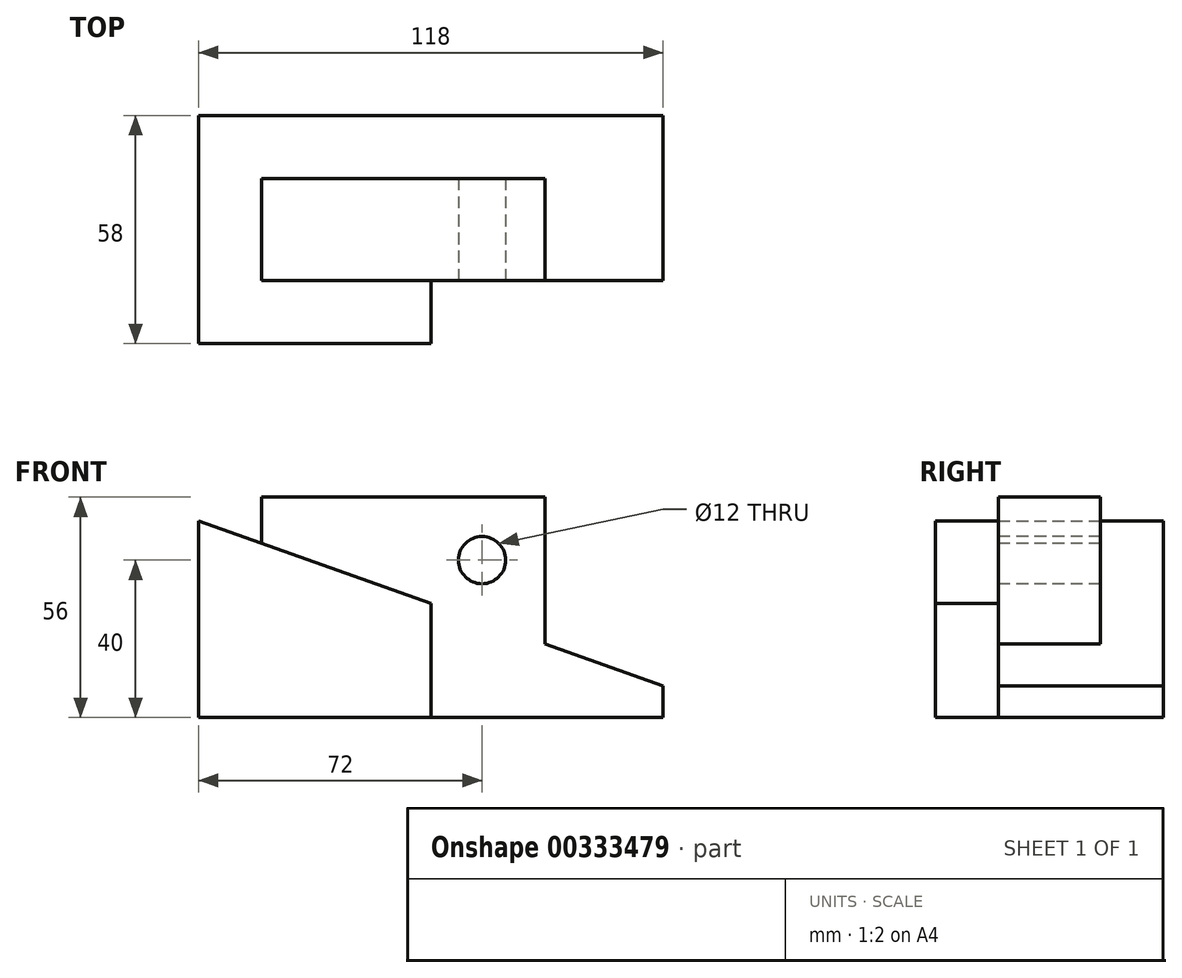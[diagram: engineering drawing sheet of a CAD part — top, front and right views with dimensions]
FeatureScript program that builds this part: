
annotation { "Feature Type Name" : "Feature", "Feature Type Description" : "" }
export const myFeature = defineFeature(function(context is Context, id is Id, definition is map)
    precondition{}
    {
        {
            var Q0;
            Q0=qCreatedBy(makeId("Front.planeOp"),FACE);
            var sketch = newSketch(context, id + "F0", { "sketchPlane" : qUnion([Q0])});
            skLineSegment(sketch, "E0", {"start": v(0, 0) * mm, "end": v(0, 50) * mm});
            skLineSegment(sketch, "E1", {"start": v(0, 50) * mm, "end": v(118, 8) * mm});
            skLineSegment(sketch, "E2", {"start": v(118, 8) * mm, "end": v(118, 0) * mm});
            skLineSegment(sketch, "E3", {"start": v(0, 0) * mm, "end": v(118, 0) * mm});
            skSolve(sketch);
        }
        {
            var Q0;
            Q0=makeQuery(id+"F0.imprint","IMPRINT",FACE,{"disambiguationData":[TD([[makeQuery(id+"F0.imprint","IMPRINT",EDGE,{"derivedFrom":sQuery(id+"F0.wireOp",EDGE,"E0")}),-1.0]])]});
            extrude(context, id + "F1", {"entities" : qUnion([Q0]), "endBound" : BoundingType.SYMMETRIC, "depth" : 58 * mm});
        }
        {
            var Q0;
            Q0=qCreatedBy(makeId("Front.planeOp"),FACE);
            var sketch = newSketch(context, id + "F2", { "sketchPlane" : qUnion([Q0])});
            skLineSegment(sketch, "E4", {"start": v(16, 44.3) * mm, "end": v(16, 56) * mm});
            skLineSegment(sketch, "E5", {"start": v(16, 56) * mm, "end": v(88, 56) * mm});
            skLineSegment(sketch, "E6", {"start": v(88, 56) * mm, "end": v(88, 18.68) * mm});
            skLineSegment(sketch, "E7", {"start": v(88, 18.68) * mm, "end": v(16, 44.3) * mm});
            skSolve(sketch);
        }
        {
            var Q0;
            Q0=makeQuery(id+"F2.imprint","IMPRINT",FACE,{"disambiguationData":[TD([[makeQuery(id+"F2.imprint","IMPRINT",EDGE,{"derivedFrom":sQuery(id+"F2.wireOp",EDGE,"E4")}),-1.0]])]});
            extrude(context, id + "F3", {"entities" : qUnion([Q0]), "operationType" : NewBodyOperationType.ADD, "endBound" : BoundingType.SYMMETRIC, "depth" : 26 * mm});
        }
        {
            var Q0;
            Q0=makeQuery(id+"F1.opExtrude","CAP_FACE",FACE,{"disambiguationData":[OSD([sQuery(id+"F0.wireOp",EDGE,"E0"),sQuery(id+"F0.wireOp",EDGE,"E1"),sQuery(id+"F0.wireOp",EDGE,"E2"),sQuery(id+"F0.wireOp",EDGE,"E3")])],"isStart":false});
            var sketch = newSketch(context, id + "F4", { "sketchPlane" : qUnion([Q0])});
            skLineSegment(sketch, "E8", {"start": v(59, 29) * mm, "end": v(59, 0) * mm});
            skLineSegment(sketch, "E9", {"start": v(59, 0) * mm, "end": v(118, 0) * mm});
            skLineSegment(sketch, "E10", {"start": v(118, 0) * mm, "end": v(118, 8) * mm});
            skLineSegment(sketch, "E11", {"start": v(118, 8) * mm, "end": v(59, 29) * mm});
            skSolve(sketch);
        }
        {
            var Q0;
            Q0=makeQuery(id+"F4.imprint","IMPRINT",FACE,{"disambiguationData":[TD([[makeQuery(id+"F4.imprint","IMPRINT",EDGE,{"derivedFrom":sQuery(id+"F4.wireOp",EDGE,"E8")}),1.0]])]});
            extrude(context, id + "F5", {"entities" : qUnion([Q0]), "operationType" : NewBodyOperationType.REMOVE, "oppositeDirection" : true, "depth" : 16 * mm});
        }
        {
            var Q0;
            Q0=makeQuery(id+"F5.boolean.opBoolean","MERGE",FACE,{"derivedFrom":[makeQuery(id+"F3.opExtrude","CAP_FACE",FACE,{"disambiguationData":[OSD([sQuery(id+"F2.wireOp",EDGE,"E4"),sQuery(id+"F2.wireOp",EDGE,"E5"),sQuery(id+"F2.wireOp",EDGE,"E6"),sQuery(id+"F2.wireOp",EDGE,"E7")])],"isStart":false}),makeQuery(id+"F5.opExtrude","CAP_FACE",FACE,{"disambiguationData":[OSD([sQuery(id+"F4.wireOp",EDGE,"E8"),sQuery(id+"F4.wireOp",EDGE,"E9"),sQuery(id+"F4.wireOp",EDGE,"E10"),sQuery(id+"F4.wireOp",EDGE,"E11")])],"isStart":false})]});
            var sketch = newSketch(context, id + "F6", { "sketchPlane" : qUnion([Q0])});
            skCircle(sketch, "E12", {"center": v(72, 40) * mm, "radius": 6 * mm});
            skSolve(sketch);
        }
        {
            var Q0;
            Q0=makeQuery(id+"F6.imprint","IMPRINT",FACE,{"disambiguationData":[TD([[makeQuery(id+"F6.imprint","IMPRINT",EDGE,{"derivedFrom":sQuery(id+"F6.wireOp",EDGE,"E12")}),1.0]])]});
            extrude(context, id + "F7", {"entities" : qUnion([Q0]), "operationType" : NewBodyOperationType.REMOVE, "endBound" : BoundingType.THROUGH_ALL, "oppositeDirection" : true, "depth" : 25 * mm});
        }
    });
